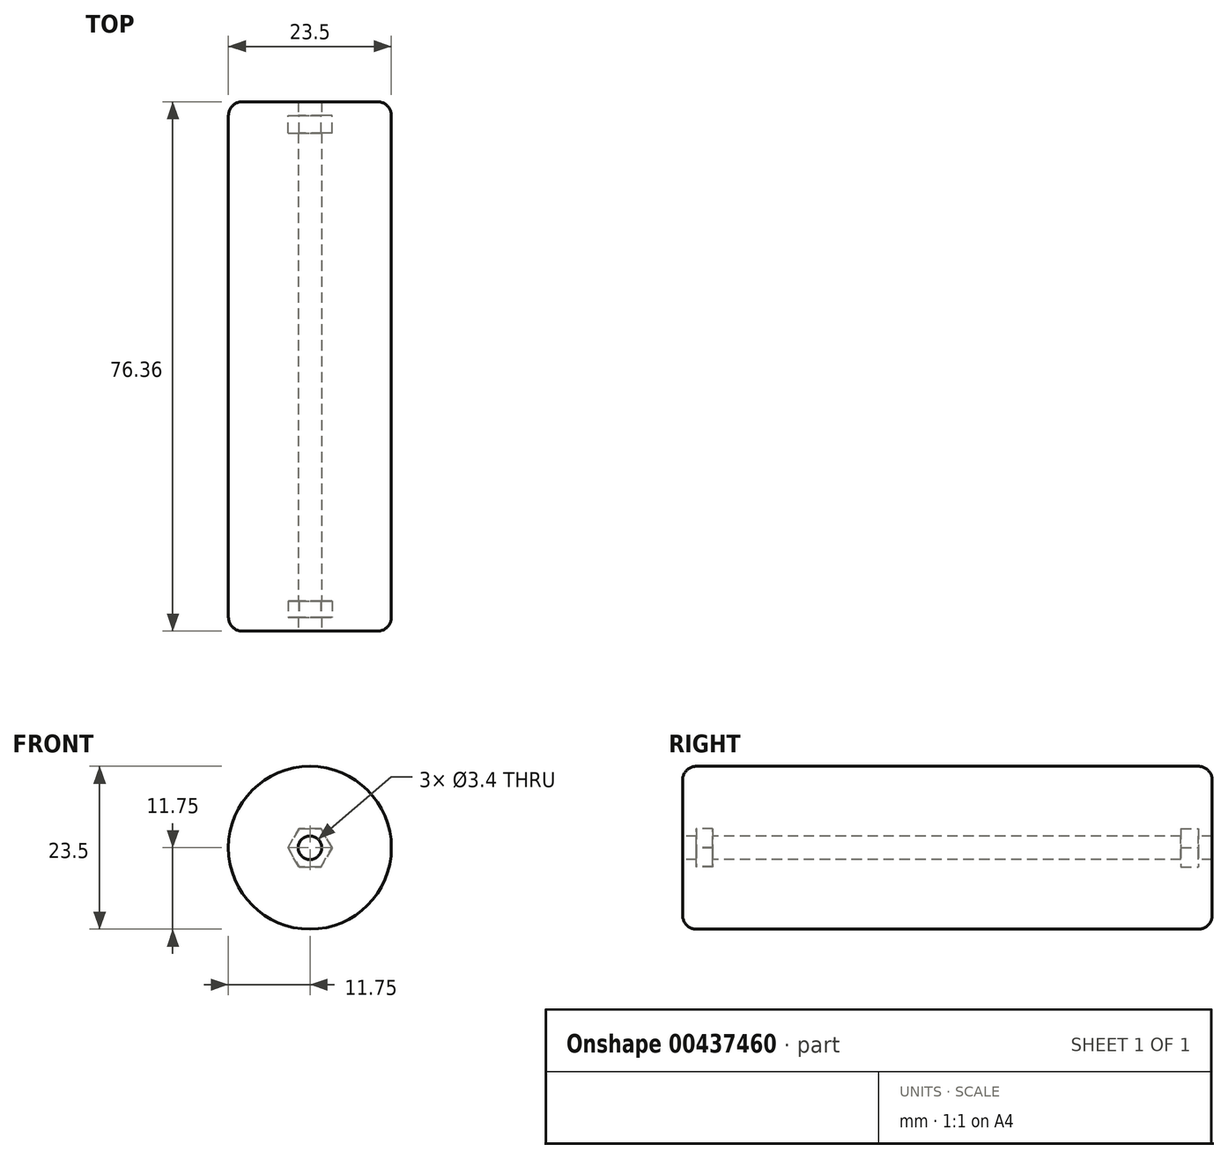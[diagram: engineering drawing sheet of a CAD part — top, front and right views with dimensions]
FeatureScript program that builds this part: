
annotation { "Feature Type Name" : "Feature", "Feature Type Description" : "" }
export const myFeature = defineFeature(function(context is Context, id is Id, definition is map)
    precondition{}
    {
        {
            var Q0;
            Q0=qCreatedBy(makeId("Front.planeOp"),FACE);
            var sketch = newSketch(context, id + "F0", { "sketchPlane" : qUnion([Q0])});
            skCircle(sketch, "E0", {"center": v(0, 0) * mm, "radius": 11.75 * mm});
            skCircle(sketch, "E1.cCircle", {"center": v(0, 0) * mm, "radius": 2.75 * mm, "construction": true});
            skLineSegment(sketch, "E1.0", {"start": v(3.18, -0.03) * mm, "end": v(1.56, -2.76) * mm});
            skLineSegment(sketch, "E1.1", {"start": v(1.56, -2.76) * mm, "end": v(-1.61, -2.74) * mm});
            skLineSegment(sketch, "E1.2", {"start": v(-1.61, -2.74) * mm, "end": v(-3.18, 0.03) * mm});
            skLineSegment(sketch, "E1.3", {"start": v(-3.18, 0.03) * mm, "end": v(-1.56, 2.76) * mm});
            skLineSegment(sketch, "E1.4", {"start": v(-1.56, 2.76) * mm, "end": v(1.61, 2.74) * mm});
            skLineSegment(sketch, "E1.5", {"start": v(1.61, 2.74) * mm, "end": v(3.18, -0.03) * mm});
            skPoint(sketch, "E1.0.midPoint", {"position": v(2.37, -1.4) * mm});
            skCircle(sketch, "E2", {"center": v(0, 0) * mm, "radius": 1.7 * mm});
            skSolve(sketch);
        }
        {
            var Q0;
            Q0=makeQuery(id+"F0.imprint","IMPRINT",FACE,{"disambiguationData":[TD([[makeQuery(id+"F0.imprint","IMPRINT",EDGE,{"derivedFrom":sQuery(id+"F0.wireOp",EDGE,"E0")}),1.0]])]});
            var Q1;
            Q1=makeQuery(id+"F0.imprint","IMPRINT",FACE,{"disambiguationData":[TD([[makeQuery(id+"F0.imprint","IMPRINT",EDGE,{"derivedFrom":sQuery(id+"F0.wireOp",EDGE,"E1.0")}),-1.0]])]});
            var Q2;
            Q2=makeQuery(id+"F0.imprint","IMPRINT",FACE,{"disambiguationData":[TD([[makeQuery(id+"F0.imprint","IMPRINT",EDGE,{"derivedFrom":sQuery(id+"F0.wireOp",EDGE,"E2")}),1.0]])]});
            extrude(context, id + "F1", {"entities" : qUnion([Q0, Q1, Q2]), "oppositeDirection" : true, "depth" : 76.36 * mm});
        }
        {
            var Q0;
            Q0=makeQuery(id+"F1.opExtrude","CAP_EDGE",EDGE,{"disambiguationData":[OSD([sQuery(id+"F0.wireOp",EDGE,"E0")])],"isStart":true});
            var Q1;
            Q1=makeQuery(id+"F1.opExtrude","CAP_EDGE",EDGE,{"disambiguationData":[OSD([sQuery(id+"F0.wireOp",EDGE,"E0")])],"isStart":false});
            fillet(context, id + "F2", {"entities" : qUnion([Q0, Q1]), "radius" : 2 * mm, "tangentPropagation" : true, "allowEdgeOverflow" : false});
        }
        {
            var Q0;
            Q0=makeQuery(id+"F0.imprint","IMPRINT",FACE,{"disambiguationData":[TD([[makeQuery(id+"F0.imprint","IMPRINT",EDGE,{"derivedFrom":sQuery(id+"F0.wireOp",EDGE,"E1.0")}),-1.0]])]});
            extrude(context, id + "F3", {"entities" : qUnion([Q0]), "operationType" : NewBodyOperationType.REMOVE, "oppositeDirection" : true, "depth" : 4.35 * mm, "hasSecondDirection" : true, "secondDirectionOppositeDirection" : true, "secondDirectionDepth" : 2 * mm});
        }
        {
            var Q0;
            Q0=makeQuery(id+"F0.imprint","IMPRINT",FACE,{"disambiguationData":[TD([[makeQuery(id+"F0.imprint","IMPRINT",EDGE,{"derivedFrom":sQuery(id+"F0.wireOp",EDGE,"E2")}),1.0]])]});
            extrude(context, id + "F4", {"entities" : qUnion([Q0]), "operationType" : NewBodyOperationType.REMOVE, "oppositeDirection" : true, "depth" : 89.7 * mm});
        }
        {
            var Q0;
            Q0=makeQuery(id+"F1.opExtrude","CAP_FACE",FACE,{"disambiguationData":[OSD([sQuery(id+"F0.wireOp",EDGE,"E0")])],"isStart":false});
            var sketch = newSketch(context, id + "F5", { "sketchPlane" : qUnion([Q0])});
            skCircle(sketch, "E3.cCircle", {"center": v(0, 0) * mm, "radius": 2.75 * mm, "construction": true});
            skLineSegment(sketch, "E3.0", {"start": v(1.59, -2.75) * mm, "end": v(-1.59, -2.75) * mm});
            skLineSegment(sketch, "E3.1", {"start": v(-1.59, -2.75) * mm, "end": v(-3.18, 0) * mm});
            skLineSegment(sketch, "E3.2", {"start": v(-3.18, 0) * mm, "end": v(-1.59, 2.75) * mm});
            skLineSegment(sketch, "E3.3", {"start": v(-1.59, 2.75) * mm, "end": v(1.59, 2.75) * mm});
            skLineSegment(sketch, "E3.4", {"start": v(1.59, 2.75) * mm, "end": v(3.18, 0) * mm});
            skLineSegment(sketch, "E3.5", {"start": v(3.18, 0) * mm, "end": v(1.59, -2.75) * mm});
            skPoint(sketch, "E3.0.midPoint", {"position": v(0, -2.75) * mm});
            skSolve(sketch);
        }
        {
            var Q0;
            Q0=makeQuery(id+"F5.imprint","IMPRINT",FACE,{"disambiguationData":[TD([[makeQuery(id+"F5.imprint","IMPRINT",EDGE,{"derivedFrom":sQuery(id+"F5.wireOp",EDGE,"E3.0")}),-1.0]])]});
            extrude(context, id + "F6", {"entities" : qUnion([Q0]), "operationType" : NewBodyOperationType.REMOVE, "oppositeDirection" : true, "depth" : 4.5 * mm, "hasSecondDirection" : true, "secondDirectionOppositeDirection" : true, "secondDirectionDepth" : 2 * mm});
        }
    });
